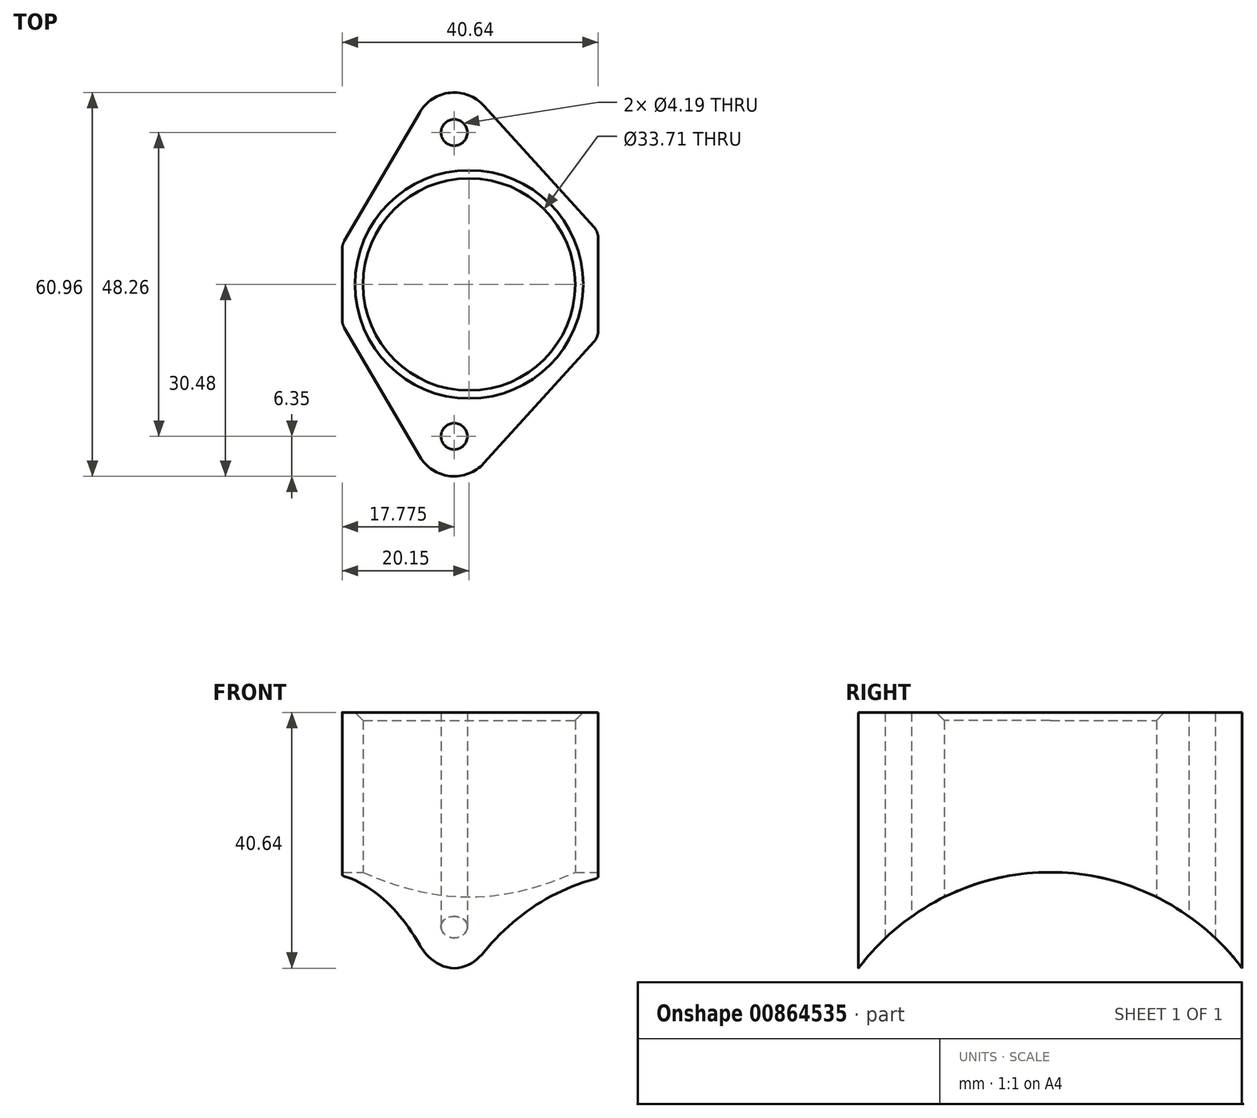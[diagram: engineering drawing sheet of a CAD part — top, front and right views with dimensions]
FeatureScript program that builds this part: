
annotation { "Feature Type Name" : "Feature", "Feature Type Description" : "" }
export const myFeature = defineFeature(function(context is Context, id is Id, definition is map)
    precondition{}
    {
        {
            var Q0;
            Q0=qCreatedBy(makeId("Top.planeOp"),FACE);
            var sketch = newSketch(context, id + "F0", { "sketchPlane" : qUnion([Q0])});
            skCircle(sketch, "E0", {"center": v(0, 0) * mm, "radius": 16.85 * mm});
            skLineSegment(sketch, "E1", {"start": v(-20.15, 6.35) * mm, "end": v(-20.15, -6.35) * mm});
            skPoint(sketch, "E2", {"position": v(-20.15, 0) * mm});
            skLineSegment(sketch, "E3", {"start": v(20.49, 8.38) * mm, "end": v(20.49, -8.38) * mm});
            skPoint(sketch, "E4", {"position": v(20.49, 0) * mm});
            skCircle(sketch, "E5", {"center": v(-2.37, 24.13) * mm, "radius": 2.1 * mm});
            skLineSegment(sketch, "E6", {"start": v(-2.37, 24.13) * mm, "end": v(-2.37, 0) * mm, "construction": true});
            skLineSegment(sketch, "E7", {"start": v(-2.37, 0) * mm, "end": v(-2.37, -24.13) * mm, "construction": true});
            skCircle(sketch, "E8", {"center": v(-2.37, -24.13) * mm, "radius": 2.1 * mm});
            skArc(sketch, "E9", {"start": v(2.33, 28.4) * mm, "mid": v(-3.03, 30.45) * mm, "end": v(-7.85, 27.34) * mm});
            skArc(sketch, "E10", {"start": v(-7.85, -27.34) * mm, "mid": v(-3.03, -30.45) * mm, "end": v(2.33, -28.4) * mm});
            skLineSegment(sketch, "E11", {"start": v(-20.15, 6.35) * mm, "end": v(-7.85, 27.34) * mm});
            skLineSegment(sketch, "E12", {"start": v(2.33, 28.4) * mm, "end": v(20.49, 8.38) * mm});
            skLineSegment(sketch, "E13", {"start": v(20.49, -8.38) * mm, "end": v(2.33, -28.4) * mm});
            skLineSegment(sketch, "E14", {"start": v(-20.15, -6.35) * mm, "end": v(-7.85, -27.34) * mm});
            skSolve(sketch);
        }
        {
            var Q0;
            Q0 = qSketchRegion(id + "F0", true);
            var Q1;
            Q1=makeQuery(id+"F0.imprint","IMPRINT",FACE,{"disambiguationData":[TD([[makeQuery(id+"F0.imprint","IMPRINT",EDGE,{"derivedFrom":sQuery(id+"F0.wireOp",EDGE,"E0")}),-1.0]])]});
            extrude(context, id + "F1", {"entities" : qUnion([Q0, Q1]), "depth" : 50.8 * mm, "offsetDistance" : 25.4 * mm});
        }
        {
            var Q0;
            Q0=qCreatedBy(makeId("Right.planeOp"),FACE);
            var sketch = newSketch(context, id + "F2", { "sketchPlane" : qUnion([Q0])});
            skCircle(sketch, "E15", {"center": v(0, -12.7) * mm, "radius": 38.1 * mm});
            skPoint(sketch, "E16", {"position": v(0, -50.8) * mm});
            skSolve(sketch);
        }
        {
            var Q0;
            Q0 = qSketchRegion(id + "F2", true);
            extrude(context, id + "F3", {"entities" : qUnion([Q0]), "operationType" : NewBodyOperationType.REMOVE, "oppositeDirection" : true, "depth" : 73.15 * mm, "offsetDistance" : 25.4 * mm, "hasSecondDirection" : true, "secondDirectionOppositeDirection" : false, "secondDirectionDepth" : 54.6 * mm});
        }
        {
            var Q0;
            Q0=makeQuery(id+"F1.opExtrude","CAP_EDGE",EDGE,{"disambiguationData":[OSD([sQuery(id+"F0.wireOp",EDGE,"E0")])],"isStart":false});
            chamfer(context, id + "F4", {"entities" : qUnion([Q0]), "width" : 1.27 * mm, "tangentPropagation" : true});
        }
        {
            var Q0;
            Q0=makeQuery(id+"F1.opExtrude","SWEPT_EDGE",EDGE,{"disambiguationData":[OSD([sQuery(id+"F0.wireOp",EDGE,"E3"),sQuery(id+"F0.wireOp",EDGE,"E12")])]});
            var Q1;
            Q1=makeQuery(id+"F1.opExtrude","SWEPT_EDGE",EDGE,{"disambiguationData":[OSD([sQuery(id+"F0.wireOp",EDGE,"E1"),sQuery(id+"F0.wireOp",EDGE,"E11")])]});
            var Q2;
            Q2=makeQuery(id+"F1.opExtrude","SWEPT_EDGE",EDGE,{"disambiguationData":[OSD([sQuery(id+"F0.wireOp",EDGE,"E1"),sQuery(id+"F0.wireOp",EDGE,"E14")])]});
            var Q3;
            Q3=makeQuery(id+"F1.opExtrude","SWEPT_EDGE",EDGE,{"disambiguationData":[OSD([sQuery(id+"F0.wireOp",EDGE,"E3"),sQuery(id+"F0.wireOp",EDGE,"E13")])]});
            fillet(context, id + "F5", {"entities" : qUnion([Q0, Q1, Q2, Q3]), "radius" : 2.54 * mm, "tangentPropagation" : true, "allowEdgeOverflow" : false});
        }
    });
